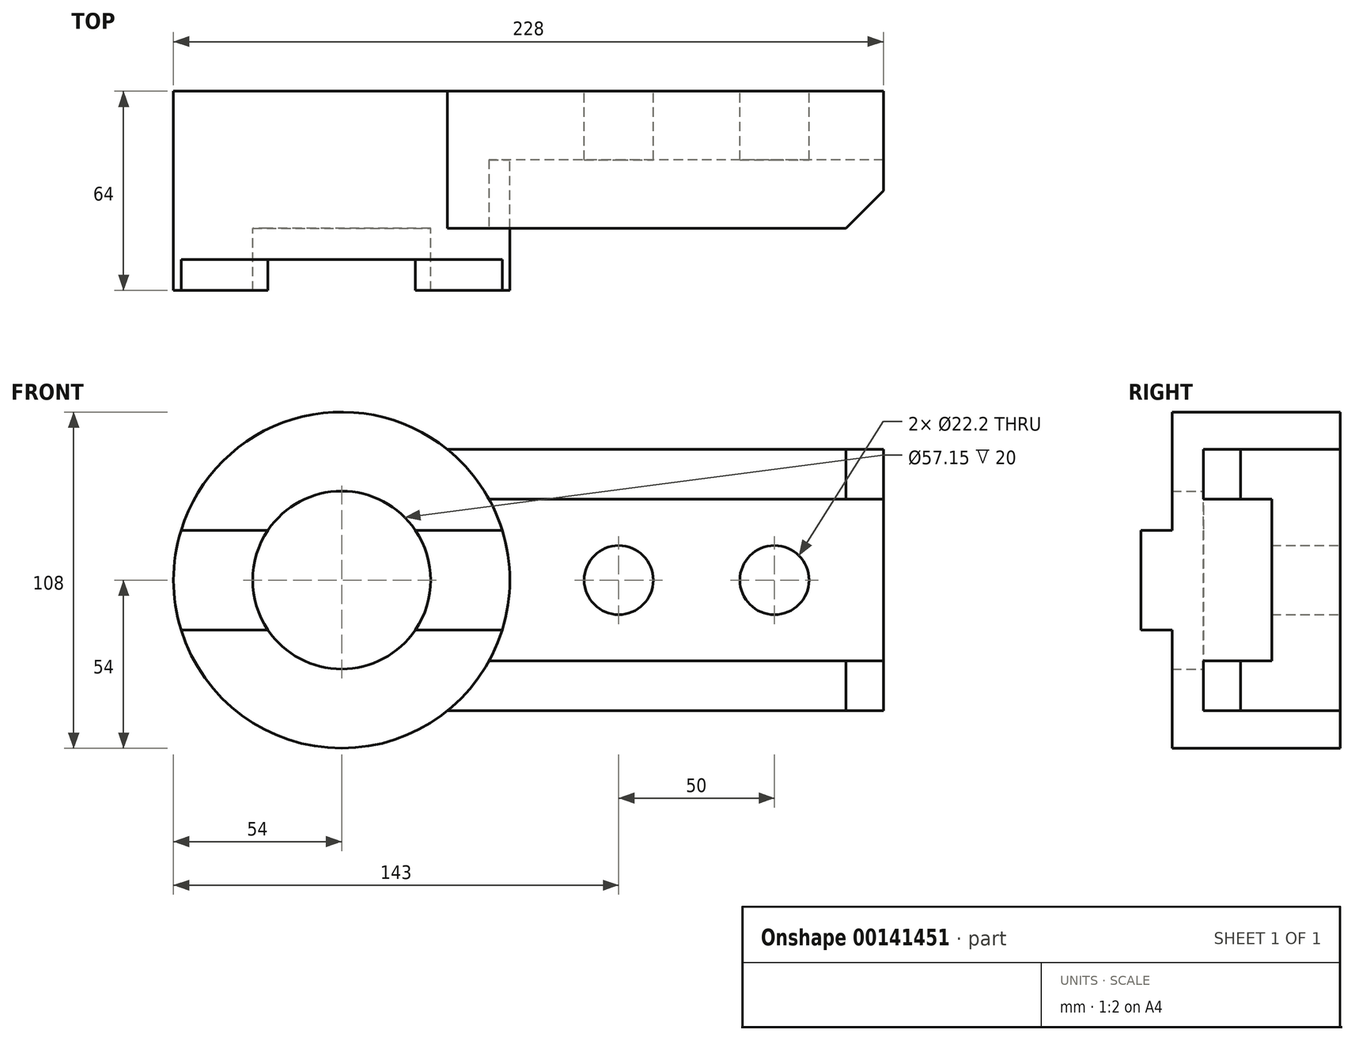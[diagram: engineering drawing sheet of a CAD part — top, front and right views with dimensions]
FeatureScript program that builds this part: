
annotation { "Feature Type Name" : "Feature", "Feature Type Description" : "" }
export const myFeature = defineFeature(function(context is Context, id is Id, definition is map)
    precondition{}
    {
        {
            var Q0;
            Q0=qCreatedBy(makeId("Front.planeOp"),FACE);
            var sketch = newSketch(context, id + "F0", { "sketchPlane" : qUnion([Q0])});
            skCircle(sketch, "E0", {"center": v(0, 0) * mm, "radius": 28.57 * mm});
            skCircle(sketch, "E1", {"center": v(0, 0) * mm, "radius": 54 * mm});
            skSolve(sketch);
        }
        {
            var Q0;
            Q0 = qSketchRegion(id + "F0", true);
            extrude(context, id + "F1", {"entities" : qUnion([Q0]), "depth" : 64 * mm});
        }
        {
            var Q0;
            Q0=qCreatedBy(makeId("Front.planeOp"),FACE);
            var sketch = newSketch(context, id + "F2", { "sketchPlane" : qUnion([Q0])});
            skCircle(sketch, "E2.0", {"center": v(0, 0) * mm, "radius": 54 * mm});
            skLineSegment(sketch, "E3", {"start": v(33.94, 42) * mm, "end": v(174, 42) * mm});
            skLineSegment(sketch, "E4", {"start": v(174, 42) * mm, "end": v(174, -42) * mm});
            skLineSegment(sketch, "E5", {"start": v(174, -42) * mm, "end": v(33.94, -42) * mm});
            skLineSegment(sketch, "E6", {"start": v(54, 0) * mm, "end": v(174, 0) * mm, "construction": true});
            skCircle(sketch, "E7", {"center": v(89, 0) * mm, "radius": 11.1 * mm});
            skCircle(sketch, "E8", {"center": v(139, 0) * mm, "radius": 11.1 * mm});
            skSolve(sketch);
        }
        {
            var Q0;
            Q0 = qSketchRegion(id + "F2", true);
            extrude(context, id + "F3", {"entities" : qUnion([Q0]), "operationType" : NewBodyOperationType.ADD, "depth" : 44 * mm});
        }
        {
            var Q0;
            Q0=makeQuery(id+"F3.opExtrude","SWEPT_FACE",FACE,{"disambiguationData":[OSD([sQuery(id+"F2.wireOp",EDGE,"E4")])]});
            var sketch = newSketch(context, id + "F4", { "sketchPlane" : qUnion([Q0])});
            skLineSegment(sketch, "E9", {"start": v(-44, 26) * mm, "end": v(-22, 26) * mm});
            skLineSegment(sketch, "E10", {"start": v(-22, 26) * mm, "end": v(-22, -26) * mm});
            skLineSegment(sketch, "E11", {"start": v(-22, -26) * mm, "end": v(-44, -26) * mm});
            skSolve(sketch);
        }
        {
            var Q0;
            {var subQ0=sQuery(id+"F2.wireOp",EDGE,"E5");var subQ1=sQuery(id+"F2.wireOp",EDGE,"E4");var subQ2=sQuery(id+"F2.wireOp",EDGE,"E3");var subQ3=sQuery(id+"F2.wireOp",EDGE,"E7");var subQ4=sQuery(id+"F2.wireOp",EDGE,"E8");Q0=makeQuery(id+"F3.boolean.opBoolean","SPLIT",FACE,{"disambiguationData":[TD([makeQuery(id+"F1.opExtrude","SWEPT_FACE",FACE,{"disambiguationData":[OSD([sQuery(id+"F0.wireOp",EDGE,"E1")])]})])],"derivedFrom":makeQuery(id+"F3.opExtrude","CAP_FACE",FACE,{"disambiguationData":[OSD([sQuery(id+"F2.wireOp",EDGE,"E2.0"),subQ2,subQ1,subQ0,subQ3,subQ4])],"isStart":false})});}
            var sketch = newSketch(context, id + "F5", { "sketchPlane" : qUnion([Q0])});
            skLineSegment(sketch, "E12.0", {"start": v(174, 26) * mm, "end": v(174, -26) * mm});
            skLineSegment(sketch, "E13", {"start": v(174, 26) * mm, "end": v(47.33, 26) * mm});
            skLineSegment(sketch, "E14", {"start": v(174, -26) * mm, "end": v(47.33, -26) * mm});
            skArc(sketch, "E15", {"start": v(47.33, -26) * mm, "mid": v(54, 0) * mm, "end": v(47.33, 26) * mm});
            skSolve(sketch);
        }
        {
            var Q0;
            Q0 = qSketchRegion(id + "F5", true);
            extrude(context, id + "F6", {"entities" : qUnion([Q0]), "operationType" : NewBodyOperationType.REMOVE, "oppositeDirection" : true, "depth" : 22 * mm});
        }
        {
            var Q0;
            Q0=makeQuery(id+"F3.opExtrude","SWEPT_FACE",FACE,{"disambiguationData":[OSD([sQuery(id+"F2.wireOp",EDGE,"E3")])]});
            var sketch = newSketch(context, id + "F7", { "sketchPlane" : qUnion([Q0])});
            skLineSegment(sketch, "E16", {"start": v(162, -44) * mm, "end": v(174, -32) * mm});
            skLineSegment(sketch, "E17.0", {"start": v(33.94, -44) * mm, "end": v(174, -44) * mm});
            skLineSegment(sketch, "E18.0", {"start": v(174, -44) * mm, "end": v(174, 0) * mm});
            skSolve(sketch);
        }
        {
            var Q0;
            Q0 = qSketchRegion(id + "F7", true);
            extrude(context, id + "F8", {"entities" : qUnion([Q0]), "operationType" : NewBodyOperationType.REMOVE, "oppositeDirection" : true, "depth" : 114.55 * mm});
        }
        {
            var Q0;
            Q0=makeQuery(id+"F1.opExtrude","CAP_FACE",FACE,{"disambiguationData":[OSD([sQuery(id+"F0.wireOp",EDGE,"E0"),sQuery(id+"F0.wireOp",EDGE,"E1")])],"isStart":false});
            var sketch = newSketch(context, id + "F9", { "sketchPlane" : qUnion([Q0])});
            skLineSegment(sketch, "E19", {"start": v(-51.58, 16) * mm, "end": v(-23.68, 16) * mm});
            skLineSegment(sketch, "E20", {"start": v(-51.58, -16) * mm, "end": v(-23.68, -16) * mm});
            skLineSegment(sketch, "E21", {"start": v(23.68, 16) * mm, "end": v(51.58, 16) * mm});
            skLineSegment(sketch, "E22", {"start": v(23.68, -16) * mm, "end": v(51.58, -16) * mm});
            skArc(sketch, "E23", {"start": v(23.68, 16) * mm, "mid": v(0, 28.57) * mm, "end": v(-23.68, 16) * mm});
            skArc(sketch, "E24", {"start": v(51.58, 16) * mm, "mid": v(0, 54) * mm, "end": v(-51.58, 16) * mm});
            skArc(sketch, "E25", {"start": v(-51.58, -16) * mm, "mid": v(0, -54) * mm, "end": v(51.58, -16) * mm});
            skArc(sketch, "E26", {"start": v(-23.68, -16) * mm, "mid": v(0, -28.58) * mm, "end": v(23.68, -16) * mm});
            skSolve(sketch);
        }
        {
            var Q0;
            Q0 = qSketchRegion(id + "F9", true);
            extrude(context, id + "F10", {"entities" : qUnion([Q0]), "operationType" : NewBodyOperationType.REMOVE, "oppositeDirection" : true, "depth" : 10 * mm});
        }
    });
